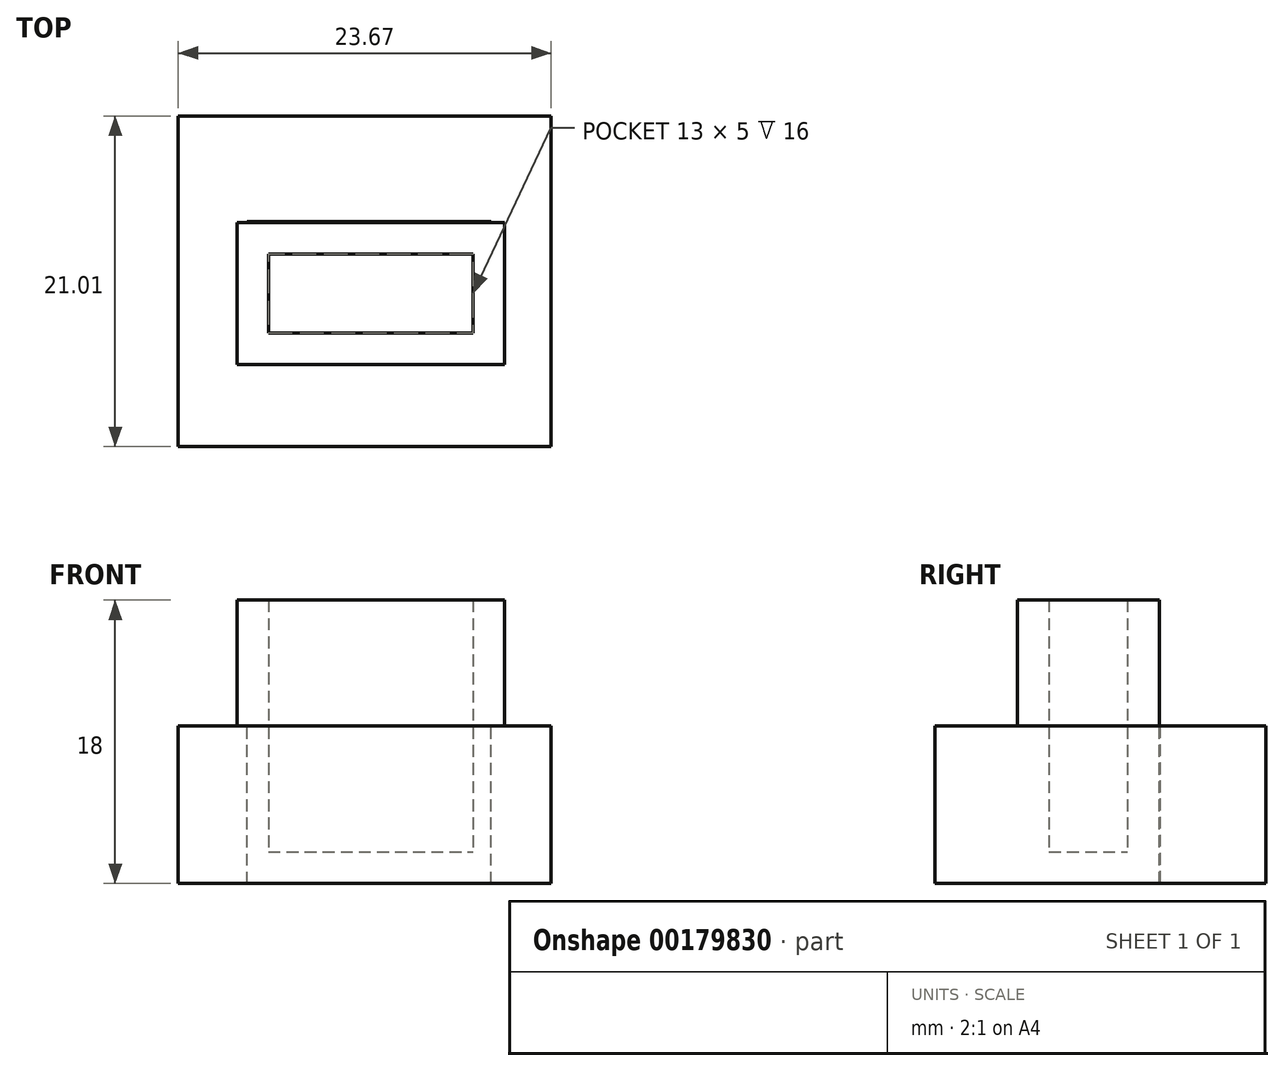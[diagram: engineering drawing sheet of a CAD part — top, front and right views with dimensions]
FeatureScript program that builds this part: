
annotation { "Feature Type Name" : "Feature", "Feature Type Description" : "" }
export const myFeature = defineFeature(function(context is Context, id is Id, definition is map)
    precondition{}
    {
        {
            var Q0;
            Q0=qCreatedBy(makeId("Top.planeOp"),FACE);
            var sketch = newSketch(context, id + "F0", { "sketchPlane" : qUnion([Q0])});
            skLineSegment(sketch, "E0", {"start": v(-25.5, 28.14) * mm, "end": v(-8.5, 28.14) * mm});
            skLineSegment(sketch, "E1", {"start": v(-8.5, 28.14) * mm, "end": v(-8.5, 19.14) * mm});
            skLineSegment(sketch, "E2", {"start": v(-8.5, 19.14) * mm, "end": v(-25.5, 19.14) * mm});
            skLineSegment(sketch, "E3", {"start": v(-25.5, 19.14) * mm, "end": v(-25.5, 28.14) * mm});
            skSolve(sketch);
        }
        {
            var Q0;
            Q0=makeQuery(id+"F0.imprint","IMPRINT",FACE,{"disambiguationData":[TD([[makeQuery(id+"F0.imprint","IMPRINT",EDGE,{"derivedFrom":sQuery(id+"F0.wireOp",EDGE,"E0")}),-1.0]])]});
            extrude(context, id + "F1", {"entities" : qUnion([Q0]), "depth" : 18 * mm});
        }
        {
            var Q0;
            Q0=makeQuery(id+"F1.opExtrude","CAP_FACE",FACE,{"disambiguationData":[OSD([sQuery(id+"F0.wireOp",EDGE,"E0"),sQuery(id+"F0.wireOp",EDGE,"E1"),sQuery(id+"F0.wireOp",EDGE,"E2"),sQuery(id+"F0.wireOp",EDGE,"E3")])],"isStart":false});
            shell(context, id + "F2", {"entities" : qUnion([Q0]), "thickness" : 2 * mm});
        }
        {
            var Q0;
            Q0=qCreatedBy(makeId("Top.planeOp"),FACE);
            var sketch = newSketch(context, id + "F3", { "sketchPlane" : qUnion([Q0])});
            skPoint(sketch, "E4.middle", {"position": v(-16.9, 23.54) * mm});
            skLineSegment(sketch, "E5", {"start": v(-24.84, 23.54) * mm, "end": v(-29.22, 23.54) * mm});
            skLineSegment(sketch, "E6", {"start": v(-29.22, 23.54) * mm, "end": v(-29.22, 28.2) * mm});
            skLineSegment(sketch, "E7", {"start": v(-29.22, 28.2) * mm, "end": v(-29.22, 34.92) * mm});
            skLineSegment(sketch, "E8", {"start": v(-29.22, 34.92) * mm, "end": v(-5.55, 34.92) * mm});
            skLineSegment(sketch, "E9", {"start": v(-5.55, 34.92) * mm, "end": v(-5.55, 23.54) * mm});
            skLineSegment(sketch, "E10", {"start": v(-5.55, 23.54) * mm, "end": v(-9.35, 23.54) * mm});
            skLineSegment(sketch, "E11", {"start": v(-9.35, 23.54) * mm, "end": v(-9.35, 28.2) * mm});
            skLineSegment(sketch, "E12", {"start": v(-24.84, 23.54) * mm, "end": v(-24.84, 28.2) * mm});
            skLineSegment(sketch, "E13", {"start": v(-24.84, 28.2) * mm, "end": v(-9.35, 28.2) * mm});
            skLineSegment(sketch, "E14", {"start": v(-24.84, 23.54) * mm, "end": v(-24.84, 19.89) * mm});
            skLineSegment(sketch, "E15", {"start": v(-24.84, 19.89) * mm, "end": v(-9.46, 19.89) * mm});
            skLineSegment(sketch, "E16", {"start": v(-9.46, 19.89) * mm, "end": v(-9.35, 23.54) * mm});
            skLineSegment(sketch, "E17", {"start": v(-29.22, 23.54) * mm, "end": v(-29.22, 13.9) * mm});
            skLineSegment(sketch, "E18", {"start": v(-29.22, 13.9) * mm, "end": v(-5.55, 13.9) * mm});
            skLineSegment(sketch, "E19", {"start": v(-5.55, 13.9) * mm, "end": v(-5.55, 23.54) * mm});
            skSolve(sketch);
        }
        {
            var Q0;
            Q0 = qSketchRegion(id + "F3", true);
            extrude(context, id + "F4", {"entities" : qUnion([Q0]), "operationType" : NewBodyOperationType.ADD, "depth" : 10 * mm});
        }
    });
